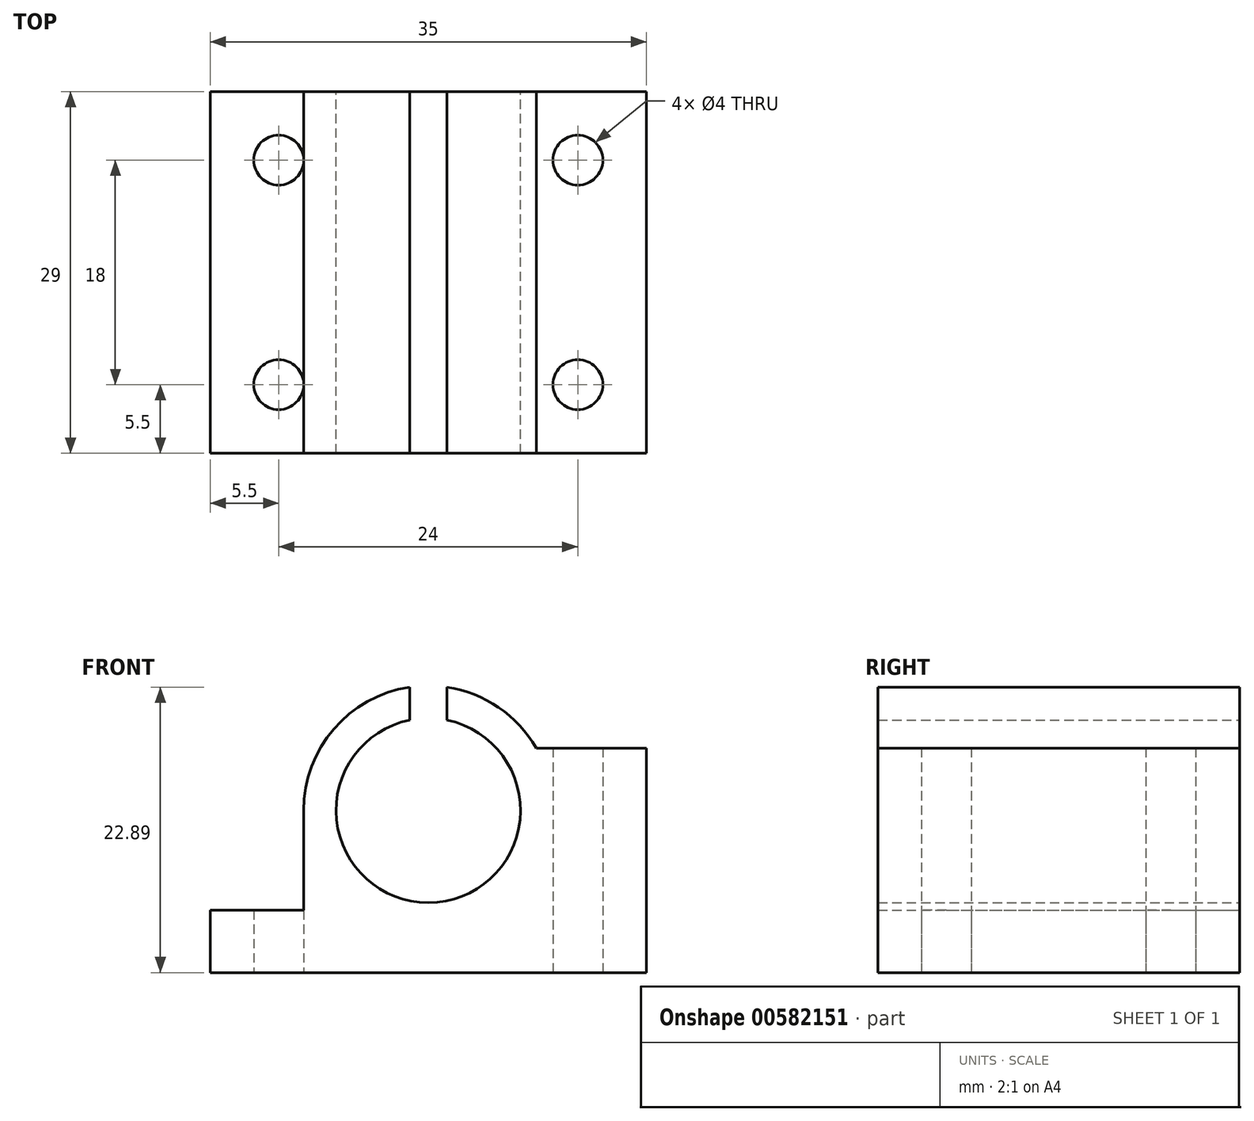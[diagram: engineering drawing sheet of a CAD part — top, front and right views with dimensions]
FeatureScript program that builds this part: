
annotation { "Feature Type Name" : "Feature", "Feature Type Description" : "" }
export const myFeature = defineFeature(function(context is Context, id is Id, definition is map)
    precondition{}
    {
        {
            var Q0;
            Q0=qCreatedBy(makeId("Front.planeOp"),FACE);
            var sketch = newSketch(context, id + "F0", { "sketchPlane" : qUnion([Q0])});
            skLineSegment(sketch, "E0", {"start": v(0, 0) * mm, "end": v(17.5, 0) * mm});
            skLineSegment(sketch, "E1", {"start": v(17.5, 0) * mm, "end": v(17.5, 5) * mm});
            skLineSegment(sketch, "E2", {"start": v(17.5, 5) * mm, "end": v(10, 5) * mm});
            skLineSegment(sketch, "E3.MirrorCS", {"start": v(-17.5, 5) * mm, "end": v(-10, 5) * mm});
            skLineSegment(sketch, "E4.MirrorCS", {"start": v(0, 0) * mm, "end": v(-17.5, 0) * mm});
            skLineSegment(sketch, "E5.MirrorCS", {"start": v(-17.5, 0) * mm, "end": v(-17.5, 5) * mm});
            skLineSegment(sketch, "E6", {"start": v(10, 5) * mm, "end": v(10, 13) * mm});
            skLineSegment(sketch, "E7", {"start": v(0, -6.19) * mm, "end": v(0, 32.8) * mm, "construction": true});
            skLineSegment(sketch, "E8.MirrorCS", {"start": v(-10, 5) * mm, "end": v(-10, 13) * mm});
            skLineSegment(sketch, "E9", {"start": v(1.5, 20.25) * mm, "end": v(1.5, 22.89) * mm});
            skArc(sketch, "E10", {"start": v(1.5, 22.89) * mm, "mid": v(7.58, 19.52) * mm, "end": v(10, 13) * mm});
            skArc(sketch, "E11", {"start": v(1.5, 20.25) * mm, "mid": v(7.36, 12.25) * mm, "end": v(0, 5.6) * mm});
            skArc(sketch, "E12.MirrorCS", {"start": v(-1.5, 22.89) * mm, "mid": v(-7.58, 19.52) * mm, "end": v(-10, 13) * mm});
            skLineSegment(sketch, "E13.MirrorCS", {"start": v(-1.5, 20.25) * mm, "end": v(-1.5, 22.89) * mm});
            skArc(sketch, "E14.MirrorCS", {"start": v(-1.5, 20.25) * mm, "mid": v(-7.36, 12.25) * mm, "end": v(0, 5.6) * mm});
            skLineSegment(sketch, "E15", {"start": v(17.5, 5) * mm, "end": v(17.5, 18) * mm});
            skLineSegment(sketch, "E16", {"start": v(17.5, 18) * mm, "end": v(8.66, 18) * mm});
            skSolve(sketch);
        }
        {
            var Q0;
            Q0=makeQuery(id+"F0.imprint","IMPRINT",FACE,{"disambiguationData":[TD([[makeQuery(id+"F0.imprint","IMPRINT",EDGE,{"derivedFrom":sQuery(id+"F0.wireOp",EDGE,"E0")}),1.0]])]});
            var Q1;
            Q1=makeQuery(id+"F0.imprint","IMPRINT",FACE,{"disambiguationData":[TD([[makeQuery(id+"F0.imprint","IMPRINT",EDGE,{"derivedFrom":sQuery(id+"F0.wireOp",EDGE,"E2")}),-1.0]])]});
            extrude(context, id + "F1", {"entities" : qUnion([Q0, Q1]), "depth" : 29 * mm, "offsetDistance" : 25 * mm});
        }
        {
            var Q0;
            Q0=makeQuery(id+"F1.opExtrude","SWEPT_FACE",FACE,{"disambiguationData":[OSD([sQuery(id+"F0.wireOp",EDGE,"E0"),sQuery(id+"F0.wireOp",EDGE,"E4.MirrorCS")])]});
            var sketch = newSketch(context, id + "F2", { "sketchPlane" : qUnion([Q0])});
            skCircle(sketch, "E17", {"center": v(-12, 23.5) * mm, "radius": 1.75 * mm});
            skLineSegment(sketch, "E18", {"start": v(0, 29) * mm, "end": v(0, -3.36) * mm, "construction": true});
            skCircle(sketch, "E19.MirrorC", {"center": v(12, 23.5) * mm, "radius": 1.75 * mm});
            skLineSegment(sketch, "E20", {"start": v(-17.5, 14.5) * mm, "end": v(22.83, 14.5) * mm, "construction": true});
            skCircle(sketch, "E21.MirrorC", {"center": v(-12, 5.5) * mm, "radius": 1.75 * mm});
            skCircle(sketch, "E22.MirrorC", {"center": v(12, 5.5) * mm, "radius": 1.75 * mm});
            skSolve(sketch);
        }
        {
            var Q0;
            Q0=sQuery(id+"F2.wireOp",VERTEX,"E17.center");
            var Q1;
            Q1=sQuery(id+"F2.wireOp",VERTEX,"E19.MirrorC.center");
            var Q2;
            Q2=sQuery(id+"F2.wireOp",VERTEX,"E21.MirrorC.center");
            var Q3;
            Q3=sQuery(id+"F2.wireOp",VERTEX,"E22.MirrorC.center");
            var Q4;
            Q4=makeQuery(id+"F1.opExtrude","SWEPT_BODY",BODY,{"disambiguationData":[OSD([sQuery(id+"F0.wireOp",EDGE,"E0"),sQuery(id+"F0.wireOp",EDGE,"E1"),sQuery(id+"F0.wireOp",EDGE,"E2"),sQuery(id+"F0.wireOp",EDGE,"Ly3XzaFO-MEAt-RE6F-LE8l-fyG6Mi8BUAm2"),sQuery(id+"F0.wireOp",EDGE,"3jlH0nAH-E49l-eZvV-lZ3N-rKZ6AzdrQb22"),sQuery(id+"F0.wireOp",EDGE,"yvDeuFeR-fRS9-B6Mu-2o3Q-hFL0JikA8Qs7"),sQuery(id+"F0.wireOp",EDGE,"E3.MirrorCS"),sQuery(id+"F0.wireOp",EDGE,"4d9fa47a-55e8-4596-9c28-741cee9445161.MirrorCS"),sQuery(id+"F0.wireOp",EDGE,"4d9fa47a-55e8-4596-9c28-741cee9445162.MirrorCS"),sQuery(id+"F0.wireOp",EDGE,"4d9fa47a-55e8-4596-9c28-741cee9445163.MirrorCS"),sQuery(id+"F0.wireOp",EDGE,"E4.MirrorCS"),sQuery(id+"F0.wireOp",EDGE,"E5.MirrorCS"),sQuery(id+"F0.wireOp",EDGE,"qFv9hw4z-pqMv-xcqi-xRy1-RO01PiSc1E5p")])]});
            hole(context, id + "F3", {"style" : HoleStyle.SIMPLE, "endStyle" : HoleEndStyle.THROUGH, "holeDiameter" : 4 * mm, "isTappedThrough" : true, "tappedDepth" : 12 * mm, "tapClearance" : 3, "locations" : qUnion([Q0, Q1, Q2, Q3]), "scope" : qUnion([Q4]), "majorDiameter" : 5 * mm});
        }
    });
